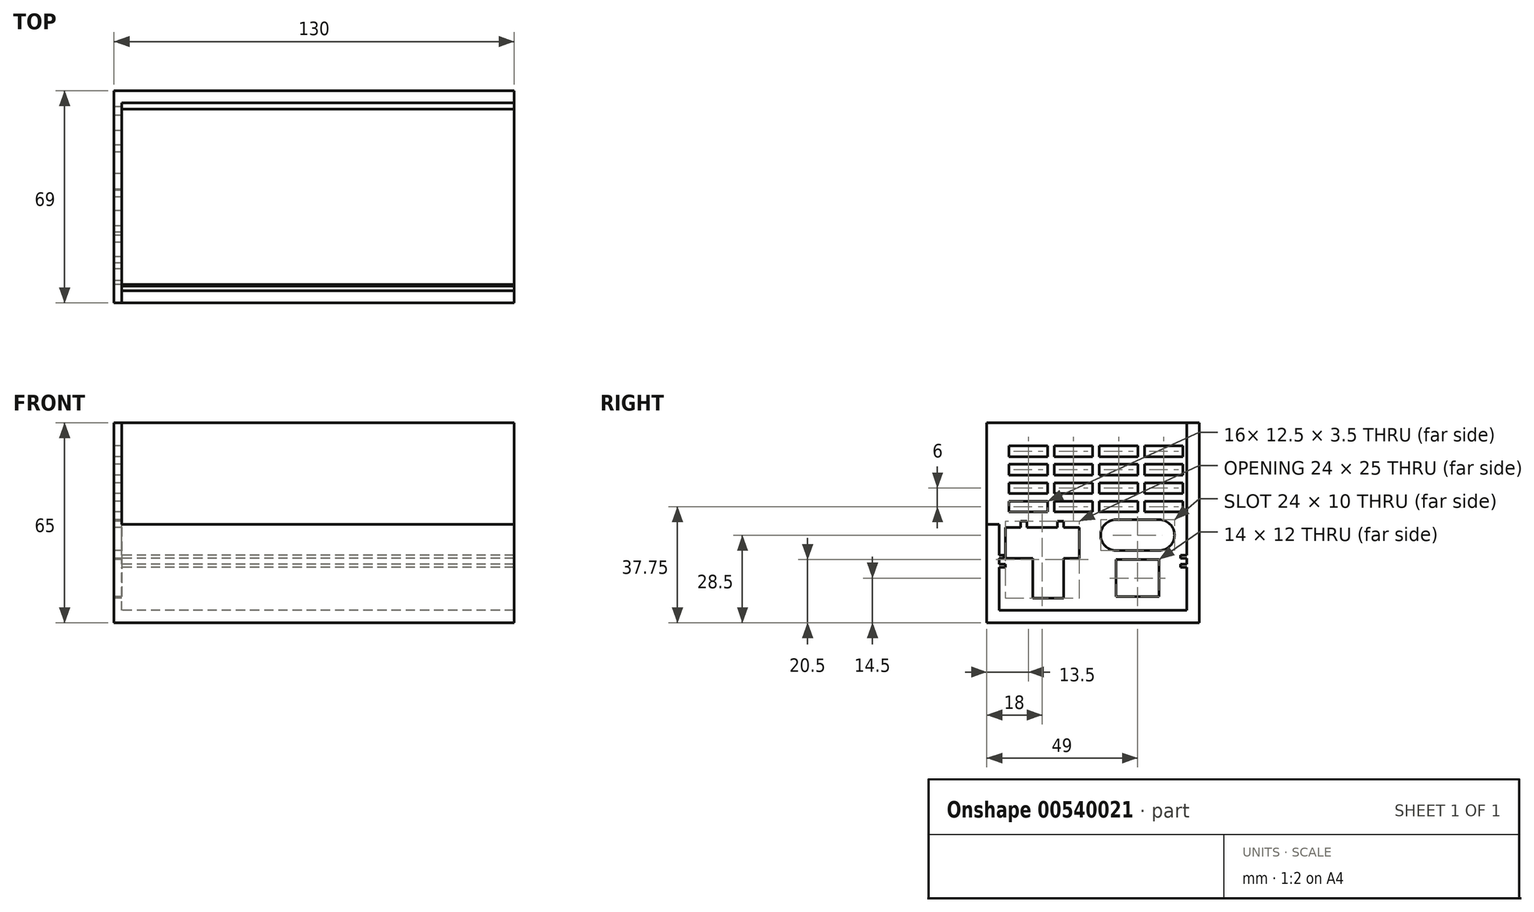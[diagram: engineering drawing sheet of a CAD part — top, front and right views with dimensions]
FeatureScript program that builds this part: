
annotation { "Feature Type Name" : "Feature", "Feature Type Description" : "" }
export const myFeature = defineFeature(function(context is Context, id is Id, definition is map)
    precondition{}
    {
        {
            var Q0;
            Q0=qCreatedBy(makeId("Right.planeOp"),FACE);
            var sketch = newSketch(context, id + "F0", { "sketchPlane" : qUnion([Q0])});
            skLineSegment(sketch, "E0", {"start": v(0, 0) * mm, "end": v(69, 0) * mm});
            skLineSegment(sketch, "E1", {"start": v(4, 4) * mm, "end": v(4, 18) * mm});
            skLineSegment(sketch, "E2", {"start": v(4, 18) * mm, "end": v(6, 18) * mm});
            skLineSegment(sketch, "E3", {"start": v(6, 18) * mm, "end": v(6, 19) * mm});
            skLineSegment(sketch, "E4", {"start": v(6, 19) * mm, "end": v(4, 19) * mm});
            skLineSegment(sketch, "E5", {"start": v(4, 19) * mm, "end": v(4, 21) * mm});
            skLineSegment(sketch, "E6", {"start": v(4, 22) * mm, "end": v(4, 32) * mm});
            skLineSegment(sketch, "E7", {"start": v(4, 32) * mm, "end": v(0, 32) * mm});
            skLineSegment(sketch, "E8", {"start": v(0, 32) * mm, "end": v(0, 0) * mm});
            skLineSegment(sketch, "E9", {"start": v(4, 4) * mm, "end": v(65, 4) * mm});
            skLineSegment(sketch, "E10", {"start": v(65, 4) * mm, "end": v(65, 18) * mm});
            skLineSegment(sketch, "E11", {"start": v(65, 4) * mm, "end": v(65, 0) * mm, "construction": true});
            skLineSegment(sketch, "E12", {"start": v(65, 19) * mm, "end": v(65, 21) * mm});
            skLineSegment(sketch, "E13", {"start": v(65, 21) * mm, "end": v(63, 21) * mm});
            skLineSegment(sketch, "E14", {"start": v(63, 21) * mm, "end": v(63, 22) * mm});
            skLineSegment(sketch, "E15", {"start": v(63, 22) * mm, "end": v(65, 22) * mm});
            skLineSegment(sketch, "E16", {"start": v(65, 22) * mm, "end": v(65, 65) * mm});
            skLineSegment(sketch, "E17", {"start": v(65, 65) * mm, "end": v(69, 65) * mm});
            skLineSegment(sketch, "E18", {"start": v(69, 65) * mm, "end": v(69, 0) * mm});
            skLineSegment(sketch, "E19", {"start": v(65, 19) * mm, "end": v(63, 19) * mm});
            skLineSegment(sketch, "E20", {"start": v(63, 19) * mm, "end": v(63, 18) * mm});
            skLineSegment(sketch, "E21", {"start": v(63, 18) * mm, "end": v(65, 18) * mm});
            skLineSegment(sketch, "E22", {"start": v(4, 22) * mm, "end": v(5.5, 22) * mm});
            skLineSegment(sketch, "E23", {"start": v(5.5, 22) * mm, "end": v(5.5, 21) * mm});
            skLineSegment(sketch, "E24", {"start": v(5.5, 21) * mm, "end": v(4, 21) * mm});
            skSolve(sketch);
        }
        {
            var Q0;
            Q0=makeQuery(id+"F0.imprint","IMPRINT",FACE,{"disambiguationData":[TD([[makeQuery(id+"F0.imprint","IMPRINT",EDGE,{"derivedFrom":sQuery(id+"F0.wireOp",EDGE,"E0")}),1.0]])]});
            extrude(context, id + "F1", {"entities" : qUnion([Q0]), "depth" : 130 * mm, "offsetDistance" : 25 * mm});
        }
        {
            var Q0;
            Q0=makeQuery(id+"F1.opExtrude","CAP_FACE",FACE,{"disambiguationData":[OSD([sQuery(id+"F0.wireOp",EDGE,"E0"),sQuery(id+"F0.wireOp",EDGE,"E1"),sQuery(id+"F0.wireOp",EDGE,"E2"),sQuery(id+"F0.wireOp",EDGE,"E3"),sQuery(id+"F0.wireOp",EDGE,"E4"),sQuery(id+"F0.wireOp",EDGE,"E5"),sQuery(id+"F0.wireOp",EDGE,"zTupMxJ7-iSA2-KNov-uvo6-SGIGFD0iAkMH"),sQuery(id+"F0.wireOp",EDGE,"tyO74KWy-AH52-Ew7G-sRGr-plD6JPyqca3a"),sQuery(id+"F0.wireOp",EDGE,"TlO4NLSi-4G3y-T53z-upQl-CTtYgG01Hu3a"),sQuery(id+"F0.wireOp",EDGE,"E6"),sQuery(id+"F0.wireOp",EDGE,"E7"),sQuery(id+"F0.wireOp",EDGE,"E8"),sQuery(id+"F0.wireOp",EDGE,"E9"),sQuery(id+"F0.wireOp",EDGE,"E10"),sQuery(id+"F0.wireOp",EDGE,"1dJf5BSC-K1NU-Keiw-R0zX-EC7QK16ufhj0"),sQuery(id+"F0.wireOp",EDGE,"gw5nfQgo-DA5u-7cWL-ZVlm-cjRol6SVNpgB"),sQuery(id+"F0.wireOp",EDGE,"CxetLdbV-gV4H-AE76-uOFp-pUmeNohf6ybg"),sQuery(id+"F0.wireOp",EDGE,"E12"),sQuery(id+"F0.wireOp",EDGE,"E13"),sQuery(id+"F0.wireOp",EDGE,"E14"),sQuery(id+"F0.wireOp",EDGE,"E15"),sQuery(id+"F0.wireOp",EDGE,"E16"),sQuery(id+"F0.wireOp",EDGE,"E17"),sQuery(id+"F0.wireOp",EDGE,"E18")])],"isStart":true});
            var sketch = newSketch(context, id + "F2", { "sketchPlane" : qUnion([Q0])});
            skLineSegment(sketch, "E25.bottom", {"start": v(0, 0) * mm, "end": v(-69, 0) * mm});
            skLineSegment(sketch, "E25.top", {"start": v(0, 65) * mm, "end": v(-69, 65) * mm});
            skLineSegment(sketch, "E25.left", {"start": v(0, 0) * mm, "end": v(0, 65) * mm});
            skLineSegment(sketch, "E25.right", {"start": v(-69, 0) * mm, "end": v(-69, 65) * mm});
            skLineSegment(sketch, "E26", {"start": v(-6, 31) * mm, "end": v(-6, 21) * mm});
            skLineSegment(sketch, "E27", {"start": v(-6, 21) * mm, "end": v(-15, 21) * mm});
            skLineSegment(sketch, "E28", {"start": v(-15, 21) * mm, "end": v(-15, 8) * mm});
            skLineSegment(sketch, "E29", {"start": v(-15, 8) * mm, "end": v(-25, 8) * mm});
            skLineSegment(sketch, "E30", {"start": v(-25, 8) * mm, "end": v(-25, 21) * mm});
            skLineSegment(sketch, "E31", {"start": v(-25, 21) * mm, "end": v(-30, 21) * mm});
            skLineSegment(sketch, "E32", {"start": v(-30, 21) * mm, "end": v(-30, 31) * mm});
            skLineSegment(sketch, "E33.bottom", {"start": v(-56, 20.5) * mm, "end": v(-42, 20.5) * mm});
            skLineSegment(sketch, "E33.top", {"start": v(-56, 8.5) * mm, "end": v(-42, 8.5) * mm});
            skLineSegment(sketch, "E33.left", {"start": v(-56, 20.5) * mm, "end": v(-56, 8.5) * mm});
            skLineSegment(sketch, "E33.right", {"start": v(-42, 20.5) * mm, "end": v(-42, 8.5) * mm});
            skLineSegment(sketch, "E34.bottom", {"start": v(-56, 23.5) * mm, "end": v(-42, 23.5) * mm});
            skLineSegment(sketch, "E34.top", {"start": v(-56, 33.5) * mm, "end": v(-42, 33.5) * mm});
            skArc(sketch, "E35", {"start": v(-42, 33.5) * mm, "mid": v(-37, 28.5) * mm, "end": v(-42, 23.5) * mm});
            skArc(sketch, "E36", {"start": v(-56, 33.5) * mm, "mid": v(-61, 28.5) * mm, "end": v(-56, 23.5) * mm});
            skLineSegment(sketch, "E37", {"start": v(-56, 20.5) * mm, "end": v(-56, 23.5) * mm, "construction": true});
            skLineSegment(sketch, "E38", {"start": v(-56, 33.5) * mm, "end": v(-56, 23.5) * mm, "construction": true});
            skLineSegment(sketch, "E39", {"start": v(-42, 33.5) * mm, "end": v(-42, 23.5) * mm, "construction": true});
            skLineSegment(sketch, "E40", {"start": v(-30, 31) * mm, "end": v(-25, 31) * mm});
            skLineSegment(sketch, "E41", {"start": v(-25, 31) * mm, "end": v(-25, 33) * mm});
            skLineSegment(sketch, "E42", {"start": v(-25, 33) * mm, "end": v(-23, 33) * mm});
            skLineSegment(sketch, "E43", {"start": v(-23, 33) * mm, "end": v(-23, 31) * mm});
            skLineSegment(sketch, "E44", {"start": v(-23, 31) * mm, "end": v(-13, 31) * mm});
            skLineSegment(sketch, "E45", {"start": v(-13, 31) * mm, "end": v(-13, 33) * mm});
            skLineSegment(sketch, "E46", {"start": v(-13, 33) * mm, "end": v(-11, 33) * mm});
            skLineSegment(sketch, "E47", {"start": v(-11, 33) * mm, "end": v(-11, 31) * mm});
            skLineSegment(sketch, "E48", {"start": v(-11, 31) * mm, "end": v(-6, 31) * mm});
            skLineSegment(sketch, "E49", {"start": v(-30, 31) * mm, "end": v(-6, 31) * mm, "construction": true});
            skLineSegment(sketch, "E50.bottom", {"start": v(-63.75, 57.5) * mm, "end": v(-51.25, 57.5) * mm});
            skLineSegment(sketch, "E50.top", {"start": v(-63.75, 54) * mm, "end": v(-51.25, 54) * mm});
            skLineSegment(sketch, "E50.left", {"start": v(-63.75, 57.5) * mm, "end": v(-63.75, 54) * mm});
            skLineSegment(sketch, "E50.right", {"start": v(-51.25, 57.5) * mm, "end": v(-51.25, 54) * mm});
            skLineSegment(sketch, "E51.1.0.0", {"start": v(-63.75, 51.5) * mm, "end": v(-51.25, 51.5) * mm});
            skLineSegment(sketch, "E51.1.0.1", {"start": v(-63.75, 51.5) * mm, "end": v(-63.75, 48) * mm});
            skLineSegment(sketch, "E51.1.0.2", {"start": v(-63.75, 48) * mm, "end": v(-51.25, 48) * mm});
            skLineSegment(sketch, "E51.1.0.3", {"start": v(-51.25, 51.5) * mm, "end": v(-51.25, 48) * mm});
            skLineSegment(sketch, "E51.2.0.0", {"start": v(-63.75, 45.5) * mm, "end": v(-51.25, 45.5) * mm});
            skLineSegment(sketch, "E51.2.0.1", {"start": v(-63.75, 45.5) * mm, "end": v(-63.75, 42) * mm});
            skLineSegment(sketch, "E51.2.0.2", {"start": v(-63.75, 42) * mm, "end": v(-51.25, 42) * mm});
            skLineSegment(sketch, "E51.2.0.3", {"start": v(-51.25, 45.5) * mm, "end": v(-51.25, 42) * mm});
            skLineSegment(sketch, "E51.3.0.0", {"start": v(-63.75, 39.5) * mm, "end": v(-51.25, 39.5) * mm});
            skLineSegment(sketch, "E51.3.0.1", {"start": v(-63.75, 39.5) * mm, "end": v(-63.75, 36) * mm});
            skLineSegment(sketch, "E51.3.0.2", {"start": v(-63.75, 36) * mm, "end": v(-51.25, 36) * mm});
            skLineSegment(sketch, "E51.3.0.3", {"start": v(-51.25, 39.5) * mm, "end": v(-51.25, 36) * mm});
            skLineSegment(sketch, "E51.direction1", {"start": v(-63.75, 54) * mm, "end": v(-63.75, 48) * mm, "construction": true});
            skLineSegment(sketch, "E52", {"start": v(-56, 33.5) * mm, "end": v(-56, 36) * mm, "construction": true});
            skLineSegment(sketch, "E53", {"start": v(-63.75, 42) * mm, "end": v(-63.75, 39.5) * mm, "construction": true});
            skLineSegment(sketch, "E54.1.0.0", {"start": v(-49.08, 57.5) * mm, "end": v(-36.58, 57.5) * mm});
            skLineSegment(sketch, "E54.1.0.1", {"start": v(-49.08, 57.5) * mm, "end": v(-49.08, 54) * mm});
            skLineSegment(sketch, "E54.1.0.2", {"start": v(-49.08, 54) * mm, "end": v(-36.58, 54) * mm});
            skLineSegment(sketch, "E54.1.0.3", {"start": v(-36.58, 57.5) * mm, "end": v(-36.58, 54) * mm});
            skLineSegment(sketch, "E54.2.0.0", {"start": v(-34.42, 57.5) * mm, "end": v(-21.92, 57.5) * mm});
            skLineSegment(sketch, "E54.2.0.1", {"start": v(-34.42, 57.5) * mm, "end": v(-34.42, 54) * mm});
            skLineSegment(sketch, "E54.2.0.2", {"start": v(-34.42, 54) * mm, "end": v(-21.92, 54) * mm});
            skLineSegment(sketch, "E54.2.0.3", {"start": v(-21.92, 57.5) * mm, "end": v(-21.92, 54) * mm});
            skLineSegment(sketch, "E54.3.0.0", {"start": v(-19.75, 57.5) * mm, "end": v(-7.25, 57.5) * mm});
            skLineSegment(sketch, "E54.3.0.1", {"start": v(-19.75, 57.5) * mm, "end": v(-19.75, 54) * mm});
            skLineSegment(sketch, "E54.3.0.2", {"start": v(-19.75, 54) * mm, "end": v(-7.25, 54) * mm});
            skLineSegment(sketch, "E54.3.0.3", {"start": v(-7.25, 57.5) * mm, "end": v(-7.25, 54) * mm});
            skLineSegment(sketch, "E54.direction1", {"start": v(-63.75, 54) * mm, "end": v(-49.08, 54) * mm, "construction": true});
            skLineSegment(sketch, "E55.1.0.0", {"start": v(-49.08, 48) * mm, "end": v(-36.58, 48) * mm});
            skLineSegment(sketch, "E55.1.0.1", {"start": v(-36.58, 51.5) * mm, "end": v(-36.58, 48) * mm});
            skLineSegment(sketch, "E55.1.0.2", {"start": v(-49.08, 51.5) * mm, "end": v(-36.58, 51.5) * mm});
            skLineSegment(sketch, "E55.1.0.3", {"start": v(-49.08, 51.5) * mm, "end": v(-49.08, 48) * mm});
            skLineSegment(sketch, "E55.2.0.0", {"start": v(-34.42, 48) * mm, "end": v(-21.92, 48) * mm});
            skLineSegment(sketch, "E55.2.0.1", {"start": v(-21.92, 51.5) * mm, "end": v(-21.92, 48) * mm});
            skLineSegment(sketch, "E55.2.0.2", {"start": v(-34.42, 51.5) * mm, "end": v(-21.92, 51.5) * mm});
            skLineSegment(sketch, "E55.2.0.3", {"start": v(-34.42, 51.5) * mm, "end": v(-34.42, 48) * mm});
            skLineSegment(sketch, "E55.3.0.0", {"start": v(-19.75, 48) * mm, "end": v(-7.25, 48) * mm});
            skLineSegment(sketch, "E55.3.0.1", {"start": v(-7.25, 51.5) * mm, "end": v(-7.25, 48) * mm});
            skLineSegment(sketch, "E55.3.0.2", {"start": v(-19.75, 51.5) * mm, "end": v(-7.25, 51.5) * mm});
            skLineSegment(sketch, "E55.3.0.3", {"start": v(-19.75, 51.5) * mm, "end": v(-19.75, 48) * mm});
            skLineSegment(sketch, "E55.direction1", {"start": v(-63.75, 48) * mm, "end": v(-49.08, 48) * mm, "construction": true});
            skLineSegment(sketch, "E56.1.0.0", {"start": v(-49.08, 45.5) * mm, "end": v(-49.08, 42) * mm});
            skLineSegment(sketch, "E56.1.0.1", {"start": v(-49.08, 42) * mm, "end": v(-36.58, 42) * mm});
            skLineSegment(sketch, "E56.1.0.2", {"start": v(-36.58, 45.5) * mm, "end": v(-36.58, 42) * mm});
            skLineSegment(sketch, "E56.1.0.3", {"start": v(-49.08, 45.5) * mm, "end": v(-36.58, 45.5) * mm});
            skLineSegment(sketch, "E56.2.0.0", {"start": v(-34.42, 45.5) * mm, "end": v(-34.42, 42) * mm});
            skLineSegment(sketch, "E56.2.0.1", {"start": v(-34.42, 42) * mm, "end": v(-21.92, 42) * mm});
            skLineSegment(sketch, "E56.2.0.2", {"start": v(-21.92, 45.5) * mm, "end": v(-21.92, 42) * mm});
            skLineSegment(sketch, "E56.2.0.3", {"start": v(-34.42, 45.5) * mm, "end": v(-21.92, 45.5) * mm});
            skLineSegment(sketch, "E56.3.0.0", {"start": v(-19.75, 45.5) * mm, "end": v(-19.75, 42) * mm});
            skLineSegment(sketch, "E56.3.0.1", {"start": v(-19.75, 42) * mm, "end": v(-7.25, 42) * mm});
            skLineSegment(sketch, "E56.3.0.2", {"start": v(-7.25, 45.5) * mm, "end": v(-7.25, 42) * mm});
            skLineSegment(sketch, "E56.3.0.3", {"start": v(-19.75, 45.5) * mm, "end": v(-7.25, 45.5) * mm});
            skLineSegment(sketch, "E56.direction1", {"start": v(-63.75, 42) * mm, "end": v(-49.08, 42) * mm, "construction": true});
            skLineSegment(sketch, "E57.1.0.0", {"start": v(-49.08, 36) * mm, "end": v(-36.58, 36) * mm});
            skLineSegment(sketch, "E57.1.0.1", {"start": v(-49.08, 39.5) * mm, "end": v(-49.08, 36) * mm});
            skLineSegment(sketch, "E57.1.0.2", {"start": v(-36.58, 39.5) * mm, "end": v(-36.58, 36) * mm});
            skLineSegment(sketch, "E57.1.0.3", {"start": v(-49.08, 39.5) * mm, "end": v(-36.58, 39.5) * mm});
            skLineSegment(sketch, "E57.2.0.0", {"start": v(-34.42, 36) * mm, "end": v(-21.92, 36) * mm});
            skLineSegment(sketch, "E57.2.0.1", {"start": v(-34.42, 39.5) * mm, "end": v(-34.42, 36) * mm});
            skLineSegment(sketch, "E57.2.0.2", {"start": v(-21.92, 39.5) * mm, "end": v(-21.92, 36) * mm});
            skLineSegment(sketch, "E57.2.0.3", {"start": v(-34.42, 39.5) * mm, "end": v(-21.92, 39.5) * mm});
            skLineSegment(sketch, "E57.3.0.0", {"start": v(-19.75, 36) * mm, "end": v(-7.25, 36) * mm});
            skLineSegment(sketch, "E57.3.0.1", {"start": v(-19.75, 39.5) * mm, "end": v(-19.75, 36) * mm});
            skLineSegment(sketch, "E57.3.0.2", {"start": v(-7.25, 39.5) * mm, "end": v(-7.25, 36) * mm});
            skLineSegment(sketch, "E57.3.0.3", {"start": v(-19.75, 39.5) * mm, "end": v(-7.25, 39.5) * mm});
            skLineSegment(sketch, "E57.direction1", {"start": v(-63.75, 36) * mm, "end": v(-49.08, 36) * mm, "construction": true});
            skSolve(sketch);
        }
        {
            var Q0;
            Q0=makeQuery(id+"F2.imprint","IMPRINT",FACE,{"disambiguationData":[TD([[makeQuery(id+"F2.imprint","IMPRINT",EDGE,{"derivedFrom":sQuery(id+"F2.wireOp",EDGE,"E26")}),1.0]])]});
            extrude(context, id + "F3", {"entities" : qUnion([Q0]), "operationType" : NewBodyOperationType.ADD, "oppositeDirection" : true, "depth" : 2.5 * mm, "offsetDistance" : 25 * mm});
        }
    });
